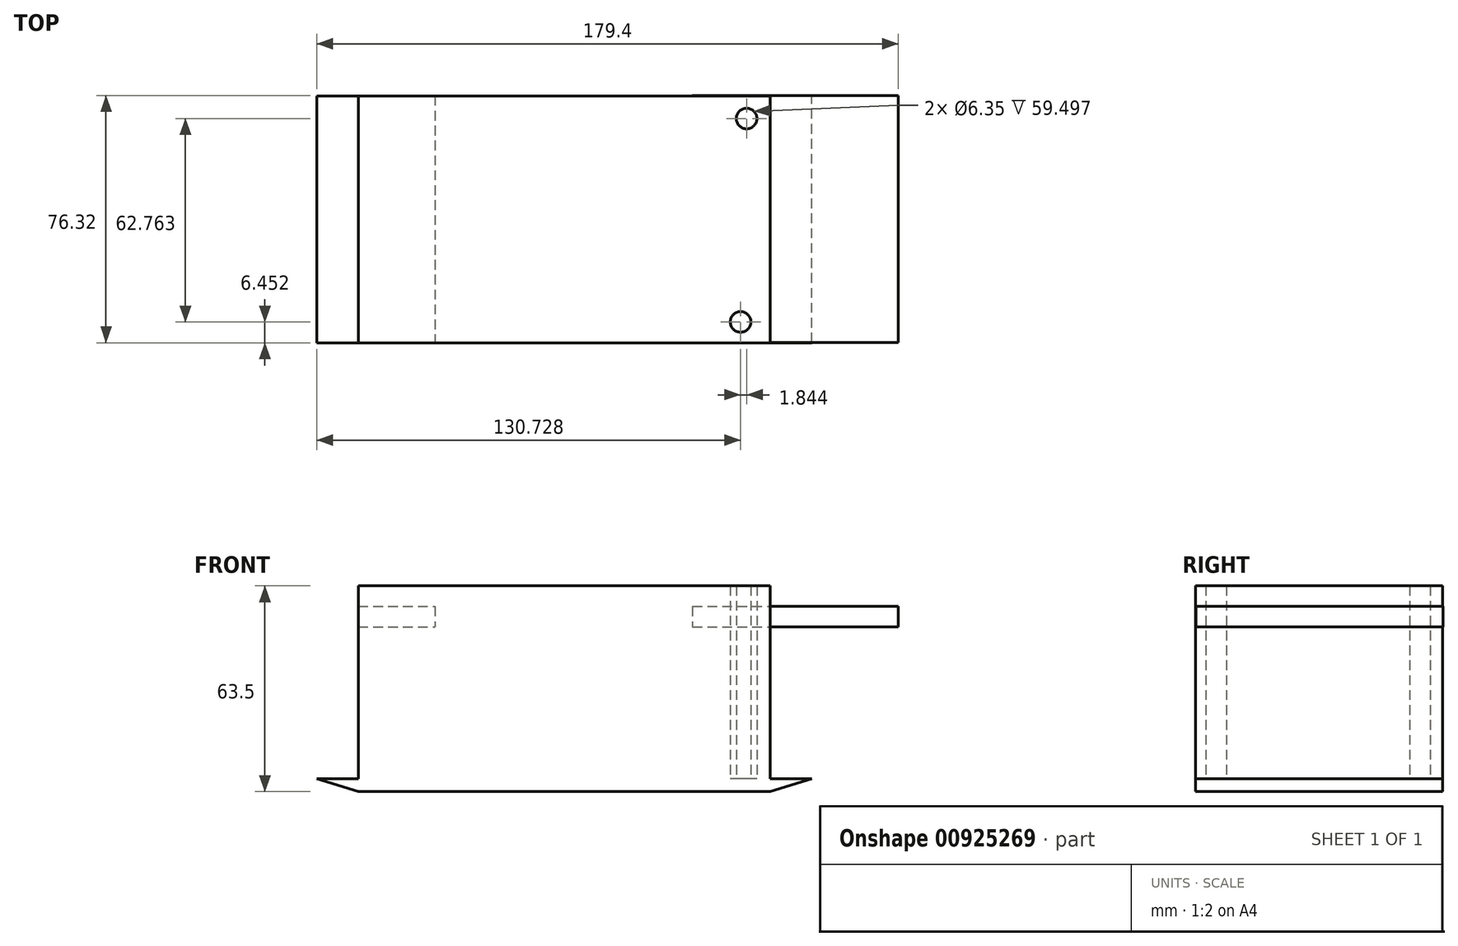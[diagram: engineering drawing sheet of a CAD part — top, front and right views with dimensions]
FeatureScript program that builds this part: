
annotation { "Feature Type Name" : "Feature", "Feature Type Description" : "" }
export const myFeature = defineFeature(function(context is Context, id is Id, definition is map)
    precondition{}
    {
        {
            var Q0;
            Q0=qCreatedBy(makeId("Front.planeOp"),FACE);
            var sketch = newSketch(context, id + "F0", { "sketchPlane" : qUnion([Q0])});
            skLineSegment(sketch, "E0", {"start": v(-63.37, 0) * mm, "end": v(63.63, 0) * mm});
            skLineSegment(sketch, "E1", {"start": v(-76.19, 4) * mm, "end": v(76.45, 4) * mm});
            skLineSegment(sketch, "E2", {"start": v(-76.19, 4) * mm, "end": v(-63.37, 0) * mm});
            skLineSegment(sketch, "E3", {"start": v(63.63, 0) * mm, "end": v(76.45, 4) * mm});
            skSolve(sketch);
        }
        {
            var Q0;
            Q0=makeQuery(id+"F0.imprint","IMPRINT",FACE,{"disambiguationData":[TD([[makeQuery(id+"F0.imprint","IMPRINT",EDGE,{"derivedFrom":sQuery(id+"F0.wireOp",EDGE,"E0")}),1.0]])]});
            extrude(context, id + "F1", {"entities" : qUnion([Q0]), "depth" : 38.1 * mm, "offsetDistance" : 25.4 * mm, "hasSecondDirection" : true, "secondDirectionOppositeDirection" : true, "secondDirectionDepth" : 38.1 * mm});
        }
        {
            var Q0;
            Q0=makeQuery(id+"F1.opExtrude","SWEPT_FACE",FACE,{"disambiguationData":[OSD([sQuery(id+"F0.wireOp",EDGE,"E0")])]});
            var sketch = newSketch(context, id + "F2", { "sketchPlane" : qUnion([Q0])});
            skCircle(sketch, "E4", {"center": v(-54.54, 31.65) * mm, "radius": 3.18 * mm});
            skLineSegment(sketch, "E5", {"start": v(0, 38.1) * mm, "end": v(0, -38.1) * mm, "construction": true});
            skCircle(sketch, "E6", {"center": v(-56.38, -31.11) * mm, "radius": 3.18 * mm});
            skCircle(sketch, "E7.MirrorC", {"center": v(54.54, 31.65) * mm, "radius": 3.18 * mm});
            skCircle(sketch, "E8.MirrorC", {"center": v(56.38, -31.11) * mm, "radius": 3.18 * mm});
            skSolve(sketch);
        }
        {
            var Q0;
            Q0=makeQuery(id+"F2.imprint","IMPRINT",FACE,{"disambiguationData":[TD([[makeQuery(id+"F2.imprint","IMPRINT",EDGE,{"derivedFrom":sQuery(id+"F2.wireOp",EDGE,"E4")}),1.0]])]});
            var Q1;
            Q1=makeQuery(id+"F2.imprint","IMPRINT",FACE,{"disambiguationData":[TD([[makeQuery(id+"F2.imprint","IMPRINT",EDGE,{"derivedFrom":sQuery(id+"F2.wireOp",EDGE,"E7.MirrorC")}),-1.0]])]});
            var Q2;
            Q2=makeQuery(id+"F2.imprint","IMPRINT",FACE,{"disambiguationData":[TD([[makeQuery(id+"F2.imprint","IMPRINT",EDGE,{"derivedFrom":sQuery(id+"F2.wireOp",EDGE,"E8.MirrorC")}),-1.0]])]});
            var Q3;
            Q3=makeQuery(id+"F2.imprint","IMPRINT",FACE,{"disambiguationData":[TD([[makeQuery(id+"F2.imprint","IMPRINT",EDGE,{"derivedFrom":sQuery(id+"F2.wireOp",EDGE,"E6")}),1.0]])]});
            extrude(context, id + "F3", {"entities" : qUnion([Q0, Q1, Q2, Q3]), "operationType" : NewBodyOperationType.ADD, "oppositeDirection" : true, "depth" : 50.8 * mm, "offsetDistance" : 25.4 * mm});
        }
        {
            var Q0;
            Q0=makeQuery(id+"F3.opExtrude","CAP_FACE",FACE,{"disambiguationData":[OSD([sQuery(id+"F2.wireOp",EDGE,"E7.MirrorC")])],"isStart":false});
            var sketch = newSketch(context, id + "F4", { "sketchPlane" : qUnion([Q0])});
            skLineSegment(sketch, "E9.bottom", {"start": v(39.7, 38.22) * mm, "end": v(103.2, 38.22) * mm});
            skLineSegment(sketch, "E9.top", {"start": v(39.7, -37.98) * mm, "end": v(103.2, -37.98) * mm});
            skLineSegment(sketch, "E9.left", {"start": v(39.7, 38.22) * mm, "end": v(39.7, -37.98) * mm});
            skLineSegment(sketch, "E9.right", {"start": v(103.2, 38.22) * mm, "end": v(103.2, -37.98) * mm});
            skLineSegment(sketch, "E10", {"start": v(0, 39.17) * mm, "end": v(0, -37.71) * mm, "construction": true});
            skLineSegment(sketch, "E11.MirrorCS", {"start": v(-39.7, 38.22) * mm, "end": v(-39.7, -37.98) * mm});
            skLineSegment(sketch, "E12.MirrorCS", {"start": v(-39.7, 38.22) * mm, "end": v(-103.2, 38.22) * mm});
            skLineSegment(sketch, "E13.MirrorCS", {"start": v(-103.2, 38.22) * mm, "end": v(-103.2, -37.98) * mm});
            skLineSegment(sketch, "E14.MirrorCS", {"start": v(-39.7, -37.98) * mm, "end": v(-103.2, -37.98) * mm});
            skSolve(sketch);
        }
        {
            var Q0;
            Q0=makeQuery(id+"F4.imprint","IMPRINT",FACE,{"disambiguationData":[TD([[makeQuery(id+"F4.imprint","IMPRINT",EDGE,{"derivedFrom":sQuery(id+"F4.wireOp",EDGE,"E9.bottom")}),-1.0]])]});
            extrude(context, id + "F5", {"entities" : qUnion([Q0]), "depth" : 6.35 * mm, "offsetDistance" : 25.4 * mm});
        }
        {
            var Q0;
            Q0=makeQuery(id+"F3.opExtrude","CAP_FACE",FACE,{"disambiguationData":[OSD([sQuery(id+"F2.wireOp",EDGE,"E7.MirrorC")])],"isStart":false});
            var Q1;
            Q1=makeQuery(id+"F3.opExtrude","CAP_FACE",FACE,{"disambiguationData":[OSD([sQuery(id+"F2.wireOp",EDGE,"E8.MirrorC")])],"isStart":false});
            var Q2;
            Q2=makeQuery(id+"F3.opExtrude","CAP_FACE",FACE,{"disambiguationData":[OSD([sQuery(id+"F2.wireOp",EDGE,"E6")])],"isStart":false});
            var Q3;
            Q3=makeQuery(id+"F3.opExtrude","CAP_FACE",FACE,{"disambiguationData":[OSD([sQuery(id+"F2.wireOp",EDGE,"E4")])],"isStart":false});
            extrude(context, id + "F6", {"entities" : qUnion([Q0, Q1, Q2, Q3]), "operationType" : NewBodyOperationType.ADD, "depth" : 12.7 * mm, "offsetDistance" : 25.4 * mm});
        }
        {
            var Q0;
            Q0=makeQuery(id+"F4.imprint","IMPRINT",FACE,{"disambiguationData":[TD([[makeQuery(id+"F4.imprint","IMPRINT",EDGE,{"derivedFrom":sQuery(id+"F4.wireOp",EDGE,"E11.MirrorCS")}),-1.0]])]});
            extrude(context, id + "F7", {"entities" : qUnion([Q0]), "depth" : 6.35 * mm, "offsetDistance" : 25.4 * mm});
        }
    });
